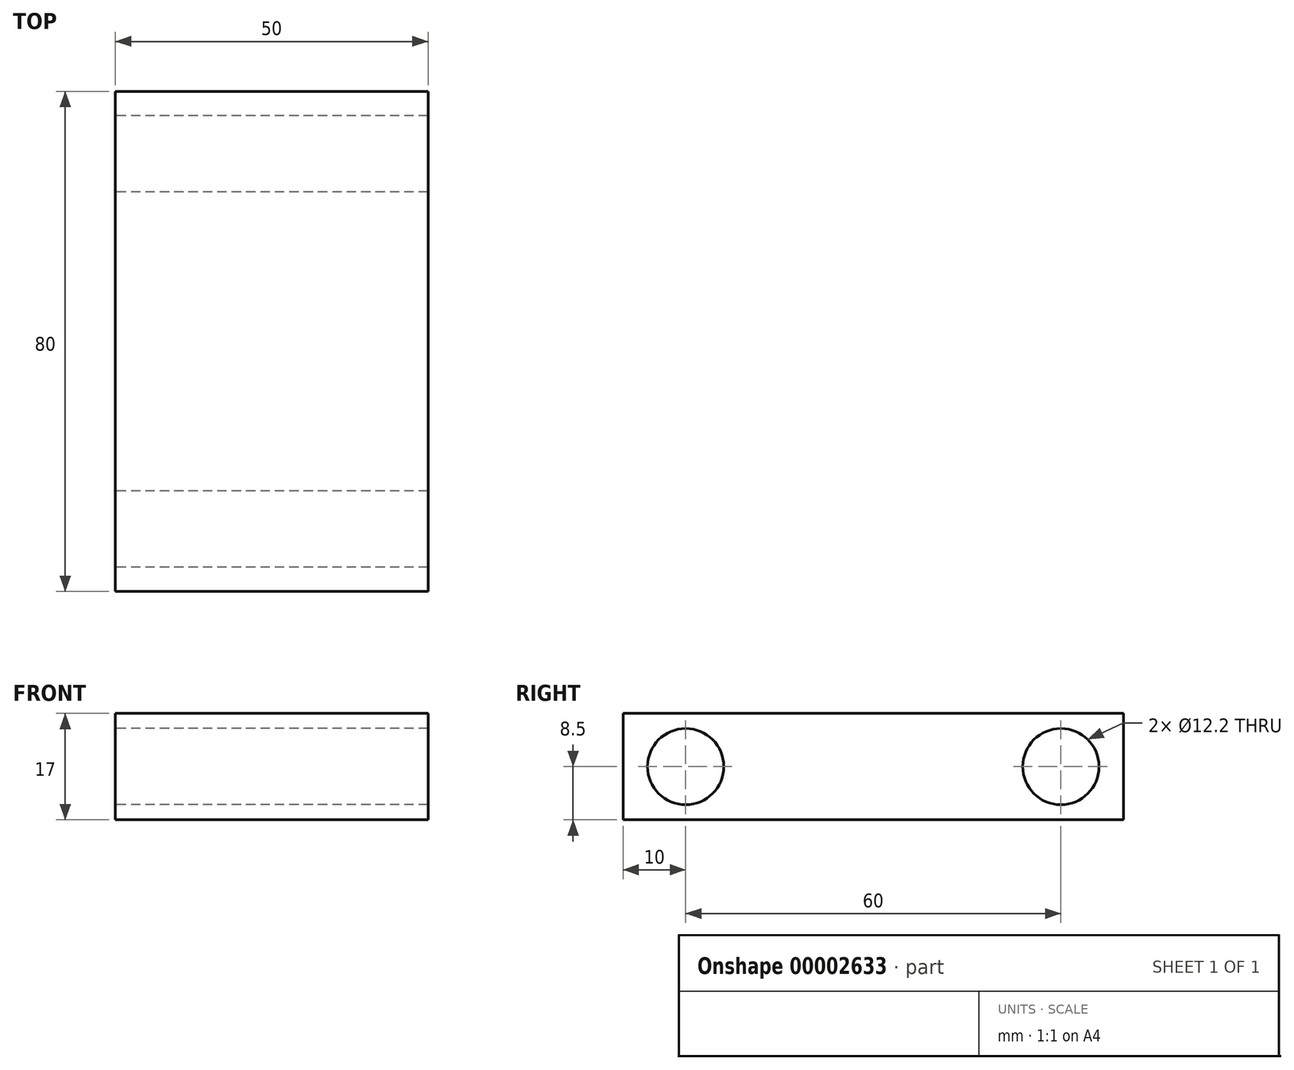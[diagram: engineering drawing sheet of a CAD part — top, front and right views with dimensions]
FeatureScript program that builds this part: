
annotation { "Feature Type Name" : "Feature", "Feature Type Description" : "" }
export const myFeature = defineFeature(function(context is Context, id is Id, definition is map)
    precondition{}
    {
        {
            var Q0;
            Q0=qCreatedBy(makeId("Right.planeOp"),FACE);
            var sketch = newSketch(context, id + "F0", { "sketchPlane" : qUnion([Q0])});
            skLineSegment(sketch, "E0", {"start": v(0, 0) * mm, "end": v(30, 0) * mm, "construction": true});
            skLineSegment(sketch, "E1", {"start": v(30, 0) * mm, "end": v(-30, 0) * mm, "construction": true});
            skCircle(sketch, "E2", {"center": v(-30, 0) * mm, "radius": 6.1 * mm});
            skCircle(sketch, "E3", {"center": v(30, 0) * mm, "radius": 6.1 * mm});
            skLineSegment(sketch, "E4.rect.bottom", {"start": v(40, -8.5) * mm, "end": v(-40, -8.5) * mm});
            skLineSegment(sketch, "E4.rect.top", {"start": v(40, 8.5) * mm, "end": v(-40, 8.5) * mm});
            skLineSegment(sketch, "E4.rect.left", {"start": v(40, -8.5) * mm, "end": v(40, 8.5) * mm});
            skLineSegment(sketch, "E4.rect.right", {"start": v(-40, -8.5) * mm, "end": v(-40, 8.5) * mm});
            skPoint(sketch, "E4.rect.middle", {"position": v(0, 0) * mm});
            skSolve(sketch);
        }
        {
            var Q0;
            Q0=makeQuery(id+"F0.imprint","IMPRINT",FACE,{"disambiguationData":[TD([[makeQuery(id+"F0.imprint","IMPRINT",EDGE,{"derivedFrom":sQuery(id+"F0.wireOp",EDGE,"E2")}),-1.0]])]});
            extrude(context, id + "F1", {"entities" : qUnion([Q0]), "depth" : 50 * mm});
        }
    });
